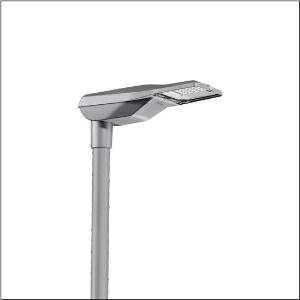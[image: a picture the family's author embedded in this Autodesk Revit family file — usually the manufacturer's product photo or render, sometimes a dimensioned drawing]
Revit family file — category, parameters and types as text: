
# Revit family: streetlight_sl_21_iq_micro___stw1_0a_5xe1e41d08cb_a1a9
name_source: partatom
category: Lighting Fixtures
units: mm (PartAtom-declared; Revit-internal decimal feet)

## family parameters
Cut with Voids When Loaded = No
Host = Face
Light Source = No
Part Type = Normal
Room Calculation Point = No
Round Connector Dimension = Use Diameter
Shared = No

## types (1)
- --- (1 x LED, 2980 lm, 19.4 W, 4000K)
    Apparent Load = 19 VA
    CIE Flux Codes = 38 75 98 100 100
    Color Rendering = 70
    Color Temperature = 4000K
    Default Elevation = 1800 mm
    Description = Streetlight SL 21 iQ micro, mast luminaire, primary light control with lens, of PMMA, primary optical cover: cover, of toughened safety glass, transparent, light distribution: STW1.0a, light emission: direct distribution, primary light characteristic: asymmetric, installation type: post-top, side-entry, LED, High Power LED, rated luminous flux: 2.980lm, luminous efficacy: 154lm/W, light colour: 740, colour temperature: 4000K, control: Auto-Match, Temp-Guard, Lumen-Switch, Night-Set, Smart-Wire, Light-Fading, Desk-Remote (wireless, voltage-free reading and setting of iQ features in the workshop via application-optimized NFC function/RFID function), optimised constant luminous flux control (CLO 2.0), presetting dimming linear, mains connection: 220..240V, AC, 50/60Hz, start of lifetime: 19W, end of service life: 20W, reduction: 10W, luminaire housing, of diecast aluminium, powder-coated, Siteco® metallic grey (DB 702S), corrosivity category C5 mid according to DIN EN ISO 12944, please order mast flange separately, inclination adjustable: 0°, 5°, 10°, 15°, sealing non-destructively replaceable, multi-level sealing system, length: 528mm, width: 235mm, height: 110mm, mast flange for spigot size: 42mm (side-entry): 5XC10008XM4, 60/48mm (side-entry/post-top): 5XC10108XM2, 76/60mm (side-entry/post-top): 5XC10108XM1, protection rating (complete): IP66, insulation class (complete): insulation class II (safety insulation), certification: CE, ENEC, ENEC+, VDE, impact resistance: IK09, permissible operating ambient temperature for outdoor applications: -40..+50°C, standard-compliant lighting for roads and squares, packaging unit: 1 piece

Light Distribution: STW1.0a
    Height = 110 mm
    Lamp = 1 x LED
    Lamp Light Flux = 2980 lm
    Lamp Power = 19.4 W
    Lamp count = 1
    Length = 528 mm
    Luminous efficacy = 154 lm/W
    Manufacturer = Siteco
    ModVariant = No
    Model = 5XE1E41D08CB
    Number of Poles = 1
    OnlyDefault = Yes
    Power Factor = 1
    Product Name = Streetlight SL 21 iQ micro | STW1.0a
    Product group = mast luminaire | pylon top
    ProductGroupID = 6100
    Protection Class = Protection class II
    Protection Degree = IP 66
    RLX_Detail_Level = 1
    RLX_Emergency_Light_Flux = 0 lm
    RLX_Emergency_Type = 0
    RLX_Emergency_Type_DB = No
    RlxData = <blob elided: 98733 chars, md5=cf25d737>
    Socket = socket
    Standby Power = 0 W
    System Light Flux = 2980 lm
    System Power = 19 W
    Type Comments = factory setting: luminous flux: 100 % | dim-lin: 254 | 387 mA
    Type Image = l_1006881.jpg
    URL = http://relux.com
    VarID = @adj_088193
    Voltage = 0 V
    Weight = 0.00 kg
    Width = 235 mm

## geometry (parser evidence)
native form markers: Blend x4, Sweep x9
no freeform markers — native parametric forms only
